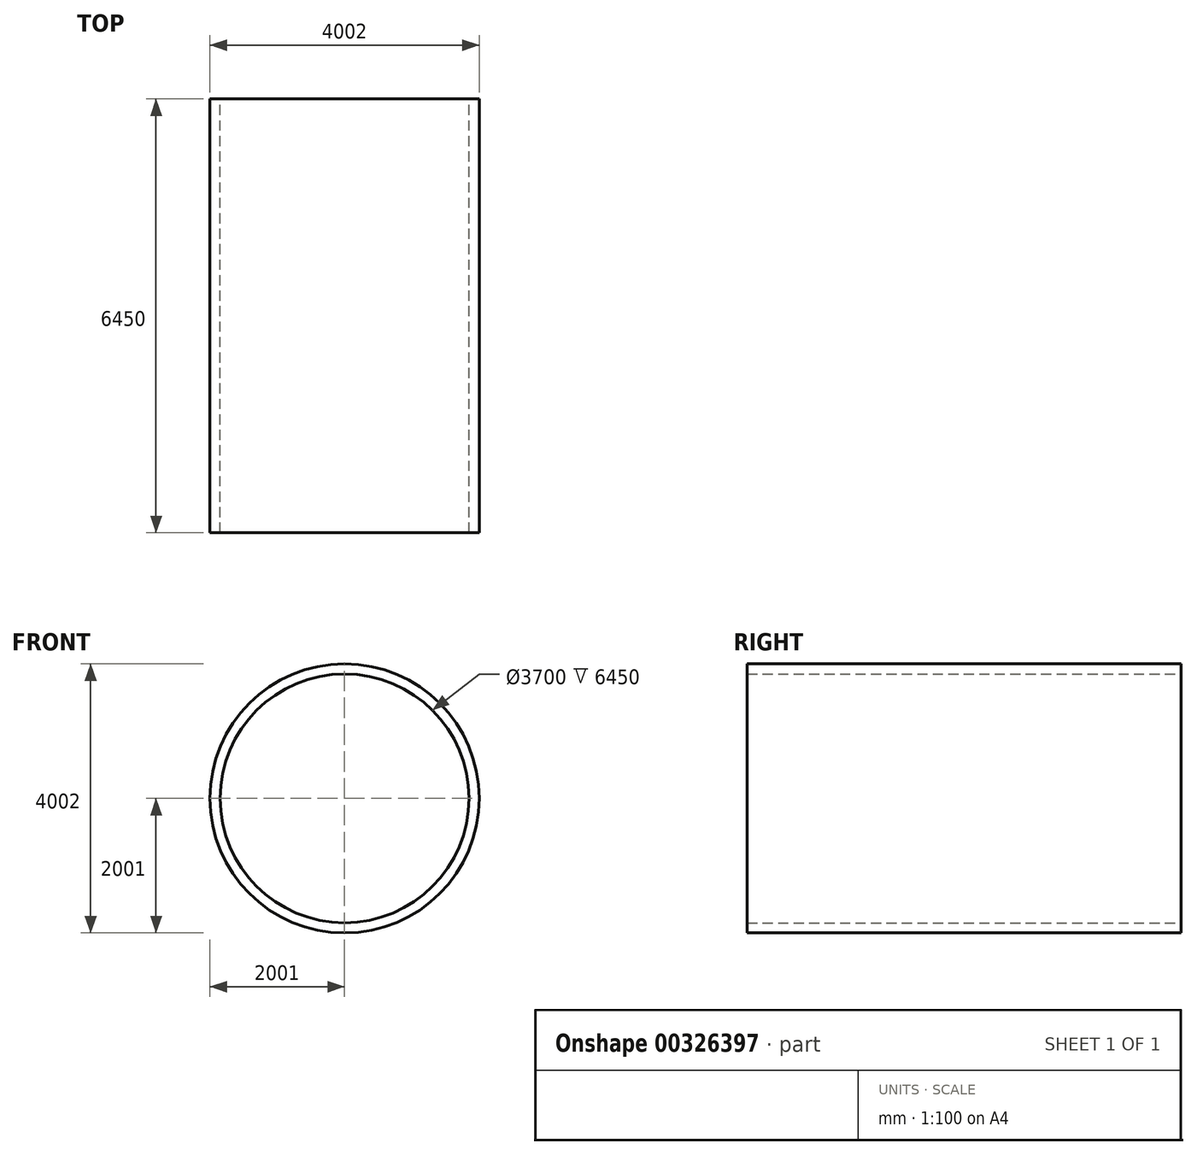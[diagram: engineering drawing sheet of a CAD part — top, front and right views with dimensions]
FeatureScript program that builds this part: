
annotation { "Feature Type Name" : "Feature", "Feature Type Description" : "" }
export const myFeature = defineFeature(function(context is Context, id is Id, definition is map)
    precondition{}
    {
        {
            var Q0;
            Q0=qCreatedBy(makeId("Front.planeOp"),FACE);
            var sketch = newSketch(context, id + "F0", { "sketchPlane" : qUnion([Q0])});
            skCircle(sketch, "E0", {"center": v(0, 0) * mm, "radius": 1850 * mm});
            skCircle(sketch, "E1.0", {"center": v(0, 0) * mm, "radius": 2001 * mm});
            skSolve(sketch);
        }
        {
            var Q0;
            Q0=makeQuery(id+"F0.imprint","IMPRINT",FACE,{"disambiguationData":[TD([[makeQuery(id+"F0.imprint","IMPRINT",EDGE,{"derivedFrom":sQuery(id+"F0.wireOp",EDGE,"E0")}),-1.0]])]});
            extrude(context, id + "F1", {"entities" : qUnion([Q0]), "depth" : 6450 * mm});
        }
    });
